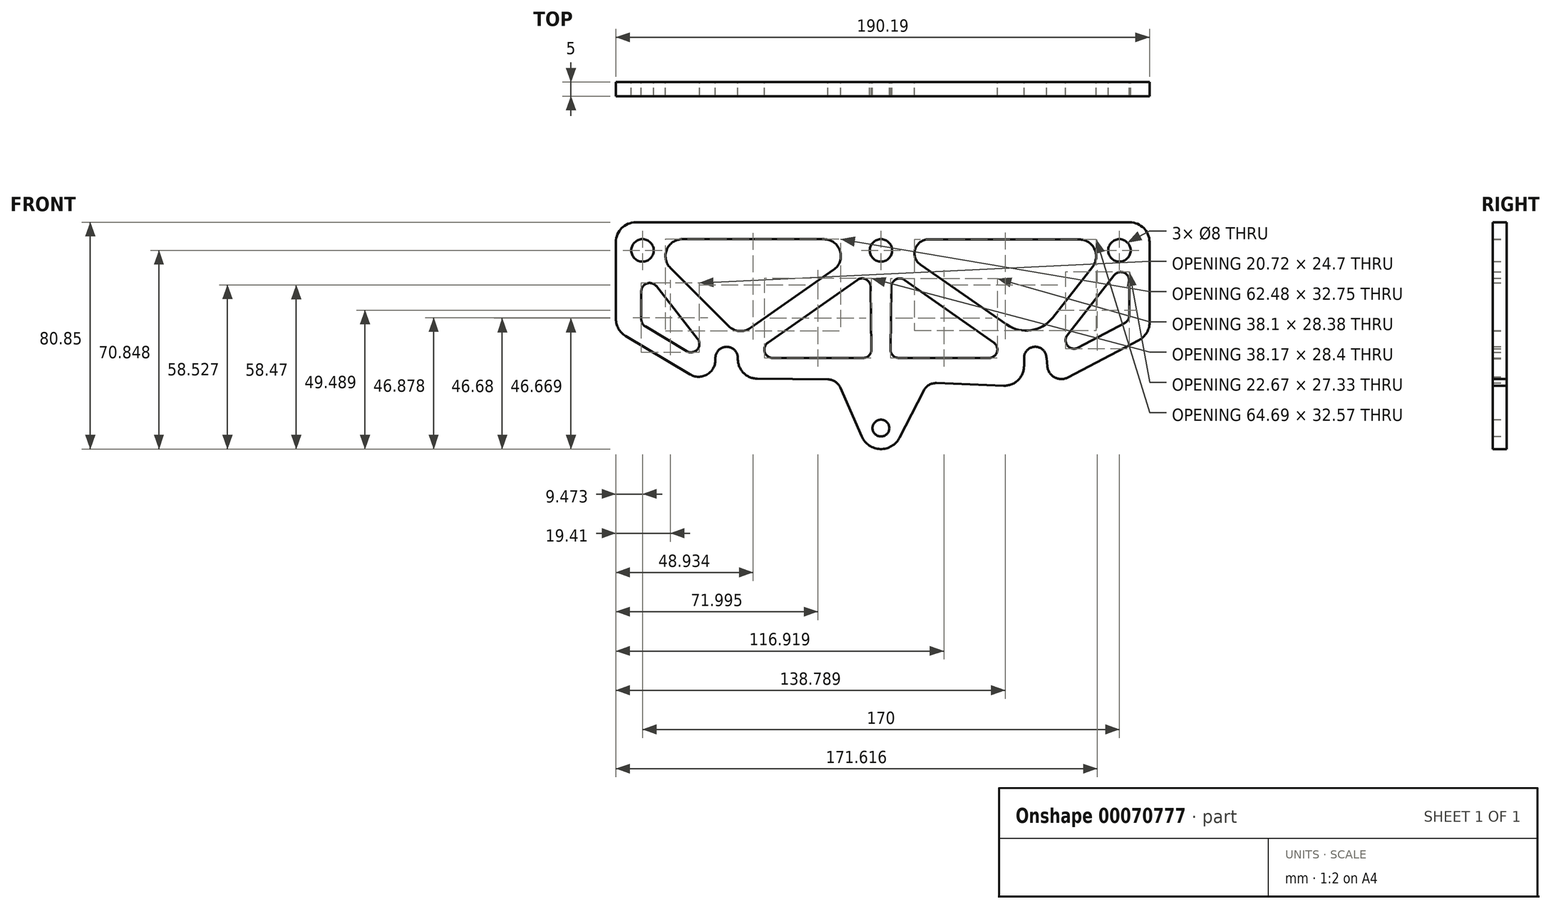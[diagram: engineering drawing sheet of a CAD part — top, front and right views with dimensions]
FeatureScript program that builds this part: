
annotation { "Feature Type Name" : "Feature", "Feature Type Description" : "" }
export const myFeature = defineFeature(function(context is Context, id is Id, definition is map)
    precondition{}
    {
        {
            var Q0;
            Q0=qCreatedBy(makeId("Front.planeOp"),FACE);
            var sketch = newSketch(context, id + "F0", { "sketchPlane" : qUnion([Q0])});
            skCircle(sketch, "E0", {"center": v(-103.94, 10) * mm, "radius": 3 * mm});
            skArc(sketch, "E1", {"start": v(-154.94, 34.95) * mm, "mid": v(-158.93, 39) * mm, "end": v(-162.94, 34.97) * mm});
            skArc(sketch, "E2", {"start": v(-44.94, 35.01) * mm, "mid": v(-49.06, 39) * mm, "end": v(-52.93, 34.77) * mm});
            skLineSegment(sketch, "E3", {"start": v(-118.42, 24.4) * mm, "end": v(-110.78, 7) * mm});
            skLineSegment(sketch, "E4", {"start": v(-88.74, 23.33) * mm, "end": v(-97.28, 6.6) * mm});
            skArc(sketch, "E5", {"start": v(-110.78, 7) * mm, "mid": v(-104.16, 2.53) * mm, "end": v(-97.28, 6.6) * mm});
            skLineSegment(sketch, "E6.trimOffspring", {"start": v(-84.1, 26.05) * mm, "end": v(-60.2, 25.13) * mm});
            skPoint(sketch, "E7.orphan", {"position": v(-38.9, 0) * mm});
            skPoint(sketch, "E8.visualSharp", {"position": v(-119.67, 27.27) * mm});
            skArc(sketch, "E8.filletArc", {"start": v(-118.42, 24.4) * mm, "mid": v(-120.18, 26.52) * mm, "end": v(-122.8, 27.39) * mm});
            skPoint(sketch, "E9.visualSharp", {"position": v(-87.29, 26.18) * mm});
            skArc(sketch, "E9.filletArc", {"start": v(-84.1, 26.05) * mm, "mid": v(-86.81, 25.37) * mm, "end": v(-88.74, 23.33) * mm});
            skPoint(sketch, "E10.visualSharp", {"position": v(-168.9, 26.14) * mm});
            skPoint(sketch, "E11.visualSharp", {"position": v(-40.44, 24.37) * mm});
            skLineSegment(sketch, "E12", {"start": v(-154.94, 34.7) * mm, "end": v(-154.94, 34.95) * mm});
            skLineSegment(sketch, "E13", {"start": v(-162.94, 35.03) * mm, "end": v(-162.94, 34.3) * mm});
            skLineSegment(sketch, "E14.trimOffspring", {"start": v(-148, 27.62) * mm, "end": v(-122.8, 27.39) * mm});
            skPoint(sketch, "E15.visualSharp", {"position": v(-162.94, 26.09) * mm});
            skPoint(sketch, "E16.visualSharp", {"position": v(-155.02, 27.68) * mm});
            skArc(sketch, "E16.filletArc", {"start": v(-154.94, 34.7) * mm, "mid": v(-152.94, 29.72) * mm, "end": v(-148, 27.62) * mm});
            skLineSegment(sketch, "E17", {"start": v(-52.93, 35.23) * mm, "end": v(-52.93, 32.13) * mm});
            skArc(sketch, "E18.filletArc", {"start": v(-60.2, 25.13) * mm, "mid": v(-55.08, 27.08) * mm, "end": v(-52.93, 32.13) * mm});
            skLineSegment(sketch, "E19", {"start": v(-44.94, 35.01) * mm, "end": v(-44.65, 32) * mm});
            skLineSegment(sketch, "E20.top", {"start": v(-191.4, 83.37) * mm, "end": v(-15.22, 83.37) * mm});
            skLineSegment(sketch, "E20.left", {"start": v(-198.4, 48.92) * mm, "end": v(-198.4, 76.37) * mm});
            skLineSegment(sketch, "E20.right", {"start": v(-8.22, 47.6) * mm, "end": v(-8.22, 76.37) * mm});
            skPoint(sketch, "E21.top.end.orphan", {"position": v(-198.4, 49.9) * mm});
            skPoint(sketch, "E22.top.end.orphan", {"position": v(-8.22, 47.85) * mm});
            skLineSegment(sketch, "E23", {"start": v(-195, 42.91) * mm, "end": v(-172.02, 29.16) * mm});
            skLineSegment(sketch, "E24", {"start": v(-11.96, 41.4) * mm, "end": v(-37.35, 28.05) * mm});
            skPoint(sketch, "E25.orphan", {"position": v(-44.35, 24.37) * mm});
            skPoint(sketch, "E26.visualSharp", {"position": v(-8.22, 43.37) * mm});
            skArc(sketch, "E26.filletArc", {"start": v(-11.96, 41.4) * mm, "mid": v(-9.22, 43.98) * mm, "end": v(-8.22, 47.6) * mm});
            skPoint(sketch, "E27.visualSharp", {"position": v(-198.4, 44.95) * mm});
            skArc(sketch, "E27.filletArc", {"start": v(-198.4, 48.92) * mm, "mid": v(-197.5, 45.46) * mm, "end": v(-195, 42.91) * mm});
            skPoint(sketch, "E28.visualSharp", {"position": v(-8.22, 83.37) * mm});
            skArc(sketch, "E28.filletArc", {"start": v(-8.22, 76.37) * mm, "mid": v(-10.27, 81.32) * mm, "end": v(-15.22, 83.37) * mm});
            skPoint(sketch, "E29.visualSharp", {"position": v(-198.4, 83.37) * mm});
            skArc(sketch, "E29.filletArc", {"start": v(-191.4, 83.37) * mm, "mid": v(-196.36, 81.32) * mm, "end": v(-198.4, 76.37) * mm});
            skArc(sketch, "E30.filletArc", {"start": v(-44.65, 32) * mm, "mid": v(-42.05, 28.08) * mm, "end": v(-37.35, 28.05) * mm});
            skCircle(sketch, "E31", {"center": v(-103.94, 73.37) * mm, "radius": 4 * mm});
            skCircle(sketch, "E32", {"center": v(-188.94, 73.37) * mm, "radius": 4 * mm});
            skCircle(sketch, "E33", {"center": v(-18.94, 73.37) * mm, "radius": 4 * mm});
            skLineSegment(sketch, "E34", {"start": v(-184, 60.6) * mm, "end": v(-169.28, 41.86) * mm});
            skPoint(sketch, "E34.endSnap0", {"position": v(-162.94, 31.09) * mm});
            skLineSegment(sketch, "E35", {"start": v(-189.36, 58.75) * mm, "end": v(-189.36, 48.82) * mm});
            skLineSegment(sketch, "E36", {"start": v(-187.9, 46.24) * mm, "end": v(-173.18, 37.44) * mm});
            skPoint(sketch, "E37.newPointA", {"position": v(-189.36, 73.37) * mm});
            skArc(sketch, "E37.filletArc", {"start": v(-184, 60.6) * mm, "mid": v(-187.34, 61.59) * mm, "end": v(-189.36, 58.75) * mm});
            skPoint(sketch, "E38.visualSharp", {"position": v(-189.36, 47.11) * mm});
            skArc(sketch, "E38.filletArc", {"start": v(-189.36, 48.82) * mm, "mid": v(-188.97, 47.34) * mm, "end": v(-187.9, 46.24) * mm});
            skPoint(sketch, "E39.newPointA", {"position": v(-162.94, 33.79) * mm});
            skArc(sketch, "E39.filletArc", {"start": v(-173.18, 37.44) * mm, "mid": v(-169.39, 38.03) * mm, "end": v(-169.28, 41.86) * mm});
            skLineSegment(sketch, "E40", {"start": v(-178.98, 67.12) * mm, "end": v(-158.16, 46.34) * mm});
            skLineSegment(sketch, "E41", {"start": v(-150.48, 45.67) * mm, "end": v(-120.8, 66.45) * mm});
            skLineSegment(sketch, "E42", {"start": v(-124.24, 77.37) * mm, "end": v(-174.74, 77.37) * mm});
            skPoint(sketch, "E43.newPointA", {"position": v(-188.25, 76.37) * mm});
            skArc(sketch, "E44.filletArc", {"start": v(-158.16, 46.34) * mm, "mid": v(-154.44, 44.61) * mm, "end": v(-150.48, 45.67) * mm});
            skArc(sketch, "E45.filletArc", {"start": v(-120.8, 66.45) * mm, "mid": v(-118.51, 73.17) * mm, "end": v(-124.24, 77.37) * mm});
            skArc(sketch, "E46.filletArc", {"start": v(-174.74, 77.37) * mm, "mid": v(-180.29, 73.66) * mm, "end": v(-178.98, 67.12) * mm});
            skPoint(sketch, "E47.newPointB", {"position": v(-162.94, 27.14) * mm});
            skArc(sketch, "E47.filletArc", {"start": v(-172.02, 29.16) * mm, "mid": v(-165.98, 29.1) * mm, "end": v(-162.94, 34.3) * mm});
            skLineSegment(sketch, "E48", {"start": v(-112.36, 62.86) * mm, "end": v(-144.23, 40.45) * mm});
            skPoint(sketch, "E49.startSnap0", {"position": v(-118.51, 73.17) * mm});
            skLineSegment(sketch, "E50", {"start": v(-95.5, 62.84) * mm, "end": v(-63.71, 40.45) * mm});
            skLineSegment(sketch, "E51.trimOffspring", {"start": v(-142.5, 35) * mm, "end": v(-110.33, 35) * mm});
            skPoint(sketch, "E52.visualSharp", {"position": v(-151.98, 35) * mm});
            skArc(sketch, "E52.filletArc", {"start": v(-144.23, 40.45) * mm, "mid": v(-145.36, 37.1) * mm, "end": v(-142.5, 35) * mm});
            skPoint(sketch, "E53.newPointA", {"position": v(-100.64, 71.1) * mm});
            skPoint(sketch, "E53.newPointB", {"position": v(-107.24, 71.1) * mm});
            skPoint(sketch, "E54.visualSharp", {"position": v(-55.97, 35) * mm});
            skArc(sketch, "E54.filletArc", {"start": v(-65.44, 35) * mm, "mid": v(-62.58, 37.1) * mm, "end": v(-63.71, 40.45) * mm});
            skLineSegment(sketch, "E55", {"start": v(-107.83, 74.28) * mm, "end": v(-107.8, 72.35) * mm});
            skLineSegment(sketch, "E56", {"start": v(-100.94, 9.93) * mm, "end": v(-100.94, 9.98) * mm});
            skLineSegment(sketch, "E57.trimOffspring", {"start": v(-107.64, 60.45) * mm, "end": v(-107.33, 38.04) * mm});
            skLineSegment(sketch, "E58.trimOffspring", {"start": v(-100.05, 72.41) * mm, "end": v(-100.03, 74.21) * mm});
            skLineSegment(sketch, "E59.trimOffspring", {"start": v(-97.54, 35) * mm, "end": v(-65.44, 35) * mm});
            skLineSegment(sketch, "E60.trimOffspring", {"start": v(-100.54, 38.04) * mm, "end": v(-100.22, 60.43) * mm});
            skPoint(sketch, "E61.visualSharp", {"position": v(-107.29, 35) * mm});
            skArc(sketch, "E61.filletArc", {"start": v(-110.33, 35) * mm, "mid": v(-108.2, 35.9) * mm, "end": v(-107.33, 38.04) * mm});
            skPoint(sketch, "E62.visualSharp", {"position": v(-100.58, 35) * mm});
            skArc(sketch, "E62.filletArc", {"start": v(-100.54, 38.04) * mm, "mid": v(-99.68, 35.9) * mm, "end": v(-97.54, 35) * mm});
            skPoint(sketch, "E63.visualSharp", {"position": v(-100.14, 66.11) * mm});
            skArc(sketch, "E63.filletArc", {"start": v(-95.5, 62.84) * mm, "mid": v(-98.59, 63.06) * mm, "end": v(-100.22, 60.43) * mm});
            skPoint(sketch, "E64.visualSharp", {"position": v(-107.72, 66.13) * mm});
            skArc(sketch, "E64.filletArc", {"start": v(-107.64, 60.45) * mm, "mid": v(-109.27, 63.08) * mm, "end": v(-112.36, 62.86) * mm});
            skCircle(sketch, "E65", {"center": v(-48.94, 35) * mm, "radius": 4 * mm});
            skLineSegment(sketch, "E66", {"start": v(-89.82, 68.23) * mm, "end": v(-59.06, 46.9) * mm});
            skLineSegment(sketch, "E67", {"start": v(-28.52, 67.55) * mm, "end": v(-42.78, 49.35) * mm});
            skLineSegment(sketch, "E68", {"start": v(-86.96, 77.33) * mm, "end": v(-33.23, 77.25) * mm});
            skLineSegment(sketch, "E69", {"start": v(-20.82, 64.52) * mm, "end": v(-37.5, 43.16) * mm});
            skArc(sketch, "E70.filletArc", {"start": v(-86.96, 77.33) * mm, "mid": v(-91.74, 73.83) * mm, "end": v(-89.82, 68.23) * mm});
            skPoint(sketch, "E71.newPointA", {"position": v(-15.22, 77.23) * mm});
            skArc(sketch, "E71.filletArc", {"start": v(-28.52, 67.55) * mm, "mid": v(-27.84, 73.88) * mm, "end": v(-33.23, 77.25) * mm});
            skArc(sketch, "E72.filletArc", {"start": v(-59.06, 46.9) * mm, "mid": v(-50.43, 44.89) * mm, "end": v(-42.78, 49.35) * mm});
            skLineSegment(sketch, "E73", {"start": v(-15.46, 62.68) * mm, "end": v(-15.46, 50.08) * mm});
            skLineSegment(sketch, "E74", {"start": v(-33.73, 38.66) * mm, "end": v(-17.06, 47.42) * mm});
            skPoint(sketch, "E74.endSnap0", {"position": v(-15.46, 52.07) * mm});
            skPoint(sketch, "E75.newPointA", {"position": v(-8.22, 52.07) * mm});
            skPoint(sketch, "E75.newPointB", {"position": v(-15.46, 28.8) * mm});
            skArc(sketch, "E75.filletArc", {"start": v(-17.06, 47.42) * mm, "mid": v(-15.89, 48.53) * mm, "end": v(-15.46, 50.08) * mm});
            skPoint(sketch, "E76.newPointB", {"position": v(-46.15, 32.13) * mm});
            skArc(sketch, "E76.filletArc", {"start": v(-37.5, 43.16) * mm, "mid": v(-37.43, 39.39) * mm, "end": v(-33.73, 38.66) * mm});
            skPoint(sketch, "E77.newPointA", {"position": v(-15.46, 71.4) * mm});
            skPoint(sketch, "E77.newPointB", {"position": v(-15.46, 75.34) * mm});
            skArc(sketch, "E77.filletArc", {"start": v(-15.46, 62.68) * mm, "mid": v(-17.48, 65.51) * mm, "end": v(-20.82, 64.52) * mm});
            skSolve(sketch);
        }
        {
            var Q0;
            Q0=makeQuery(id+"F0.imprint","IMPRINT",FACE,{"disambiguationData":[TD([[makeQuery(id+"F0.imprint","IMPRINT",EDGE,{"derivedFrom":sQuery(id+"F0.wireOp",EDGE,"E0")}),-1.0]])]});
            extrude(context, id + "F1", {"entities" : qUnion([Q0]), "flatOperationType" : FlatOperationType.REMOVE, "offsetDistance" : 25 * mm, "depth" : 5 * mm, "domain" : OperationDomain.MODEL});
        }
    });
